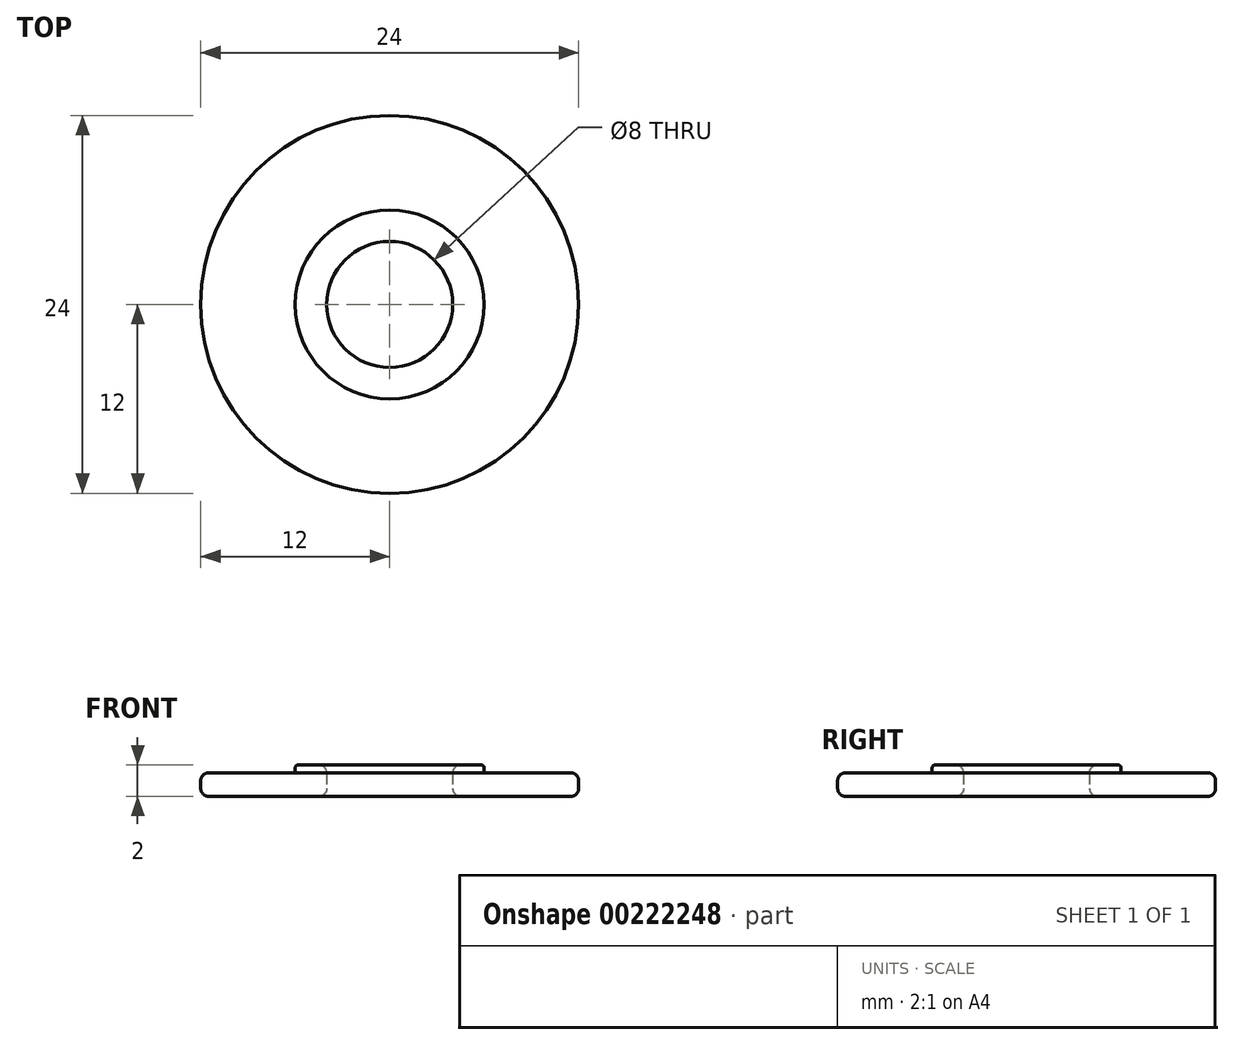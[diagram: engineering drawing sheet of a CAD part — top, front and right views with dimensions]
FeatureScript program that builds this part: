
annotation { "Feature Type Name" : "Feature", "Feature Type Description" : "" }
export const myFeature = defineFeature(function(context is Context, id is Id, definition is map)
    precondition{}
    {
        {
            var Q0;
            Q0=qCreatedBy(makeId("Top.planeOp"),FACE);
            var sketch = newSketch(context, id + "F0", { "sketchPlane" : qUnion([Q0])});
            skCircle(sketch, "E0", {"center": v(0, 0) * mm, "radius": 12 * mm});
            skCircle(sketch, "E1", {"center": v(0, 0) * mm, "radius": 4 * mm});
            skCircle(sketch, "E2", {"center": v(0, 0) * mm, "radius": 6 * mm});
            skSolve(sketch);
        }
        {
            var Q0;
            Q0=makeQuery(id+"F0.imprint","IMPRINT",FACE,{"disambiguationData":[TD([[makeQuery(id+"F0.imprint","IMPRINT",EDGE,{"derivedFrom":sQuery(id+"F0.wireOp",EDGE,"E1")}),-1.0]])]});
            extrude(context, id + "F1", {"entities" : qUnion([Q0]), "depth" : 2 * mm});
        }
        {
            var Q0;
            Q0=qSketchRegion(id+"F0",true);
            extrude(context, id + "F2", {"entities" : qUnion([Q0]), "operationType" : NewBodyOperationType.ADD, "depth" : 1.5 * mm});
        }
        {
            var Q0;
            Q0=makeQuery(id+"F2.opExtrude","CAP_EDGE",EDGE,{"disambiguationData":[OSD([sQuery(id+"F0.wireOp",EDGE,"E0")])],"isStart":false});
            fillet(context, id + "F3", {"entities" : qUnion([Q0]), "radius" : 0.5 * mm, "tangentPropagation" : true, "allowEdgeOverflow" : false});
        }
        {
            var Q0;
            Q0=makeQuery(id+"F2.opExtrude","CAP_EDGE",EDGE,{"disambiguationData":[OSD([sQuery(id+"F0.wireOp",EDGE,"E2")])],"isStart":false});
            var Q1;
            Q1=makeQuery(id+"F1.opExtrude","CAP_EDGE",EDGE,{"disambiguationData":[OSD([sQuery(id+"F0.wireOp",EDGE,"E2")])],"isStart":false});
            fillet(context, id + "F4", {"entities" : qUnion([Q0, Q1]), "radius" : 0.2 * mm, "tangentPropagation" : true, "allowEdgeOverflow" : false});
        }
        {
            var Q0;
            Q0=makeQuery(id+"F2.opExtrude","CAP_EDGE",EDGE,{"disambiguationData":[OSD([sQuery(id+"F0.wireOp",EDGE,"E0")])],"isStart":true});
            var Q1;
            Q1=makeQuery(id+"F1.opExtrude","CAP_EDGE",EDGE,{"disambiguationData":[OSD([sQuery(id+"F0.wireOp",EDGE,"E1")])],"isStart":true});
            var Q2;
            Q2=makeQuery(id+"F1.opExtrude","CAP_EDGE",EDGE,{"disambiguationData":[OSD([sQuery(id+"F0.wireOp",EDGE,"E1")])],"isStart":false});
            fillet(context, id + "F5", {"entities" : qUnion([Q0, Q1, Q2]), "radius" : 0.5 * mm, "tangentPropagation" : true, "allowEdgeOverflow" : false});
        }
    });
